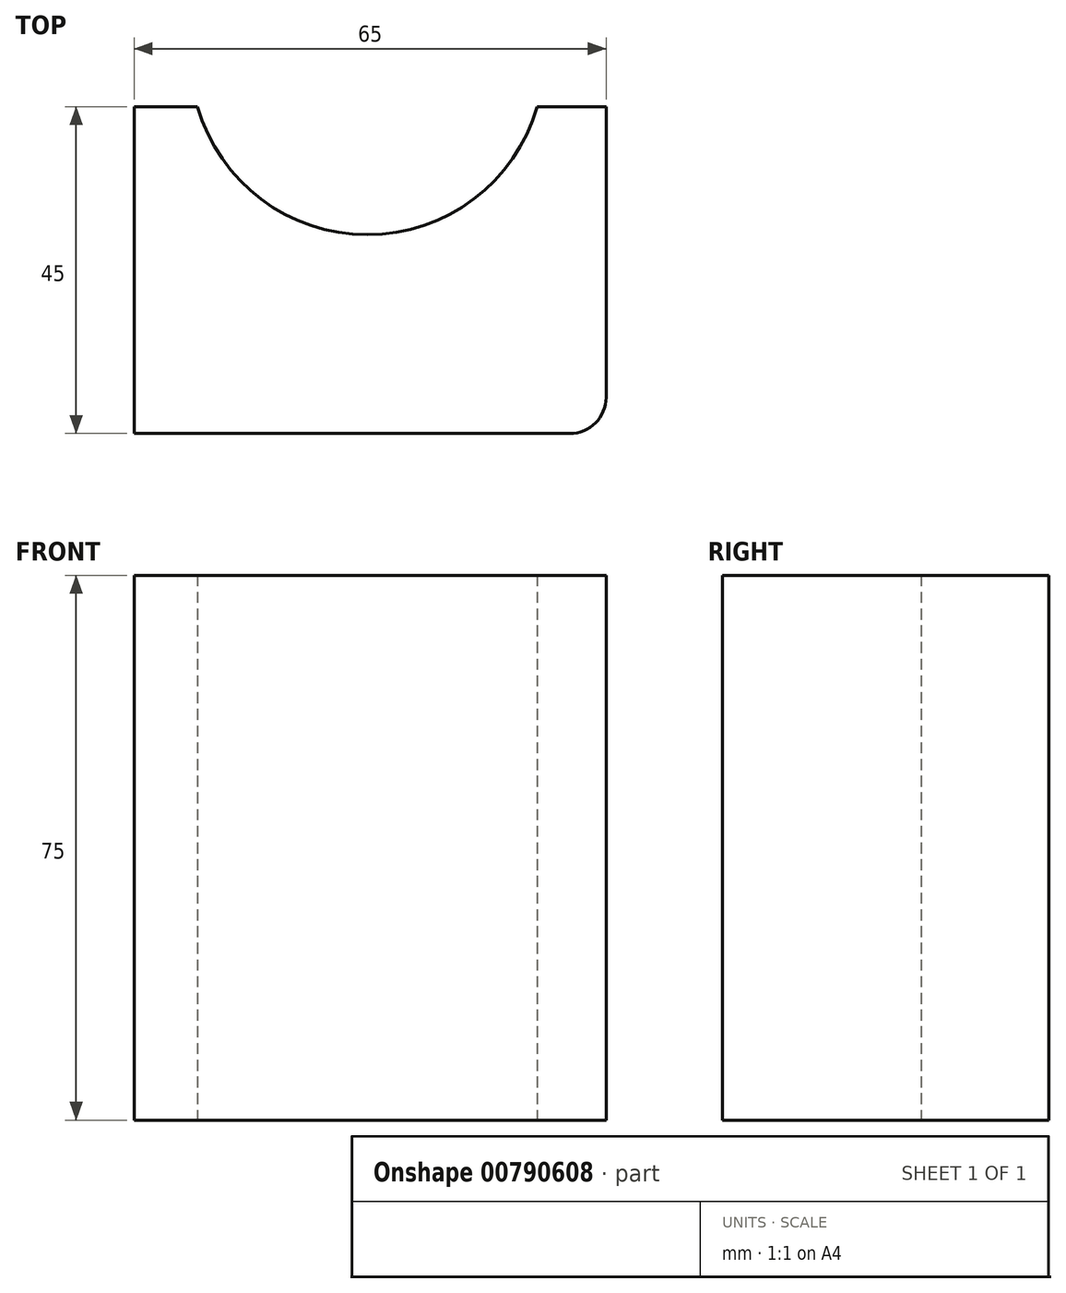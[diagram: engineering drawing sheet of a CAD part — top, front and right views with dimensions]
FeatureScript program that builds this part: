
annotation { "Feature Type Name" : "Feature", "Feature Type Description" : "" }
export const myFeature = defineFeature(function(context is Context, id is Id, definition is map)
    precondition{}
    {
        {
            var Q0;
            Q0=qCreatedBy(makeId("Top.planeOp"),FACE);
            var sketch = newSketch(context, id + "F0", { "sketchPlane" : qUnion([Q0])});
            skLineSegment(sketch, "E0.bottom", {"start": v(-23.67, -18.66) * mm, "end": v(41.33, -18.66) * mm});
            skLineSegment(sketch, "E0.top", {"start": v(-23.67, 26.34) * mm, "end": v(41.33, 26.34) * mm});
            skLineSegment(sketch, "E0.left", {"start": v(-23.67, -18.66) * mm, "end": v(-23.67, 26.34) * mm});
            skLineSegment(sketch, "E0.right", {"start": v(41.33, -18.66) * mm, "end": v(41.33, 26.34) * mm});
            skCircle(sketch, "E1", {"center": v(8.45, 33.05) * mm, "radius": 24.34 * mm});
            skSolve(sketch);
        }
        {
            var Q0;
            Q0=makeQuery(id+"F0.imprint","IMPRINT",FACE,{"disambiguationData":[TD([[makeQuery(id+"F0.imprint","IMPRINT",EDGE,{"derivedFrom":sQuery(id+"F0.wireOp",EDGE,"E0.bottom")}),1.0]])]});
            extrude(context, id + "F1", {"entities" : qUnion([Q0]), "depth" : 75 * mm, "offsetDistance" : 25 * mm});
        }
        {
            var Q0;
            Q0=makeQuery(id+"F1.opExtrude","SWEPT_EDGE",EDGE,{"disambiguationData":[OSD([sQuery(id+"F0.wireOp",EDGE,"E0.bottom"),sQuery(id+"F0.wireOp",EDGE,"E0.right")])]});
            fillet(context, id + "F2", {"entities" : qUnion([Q0]), "radius" : 5 * mm, "tangentPropagation" : true, "allowEdgeOverflow" : false});
        }
    });
